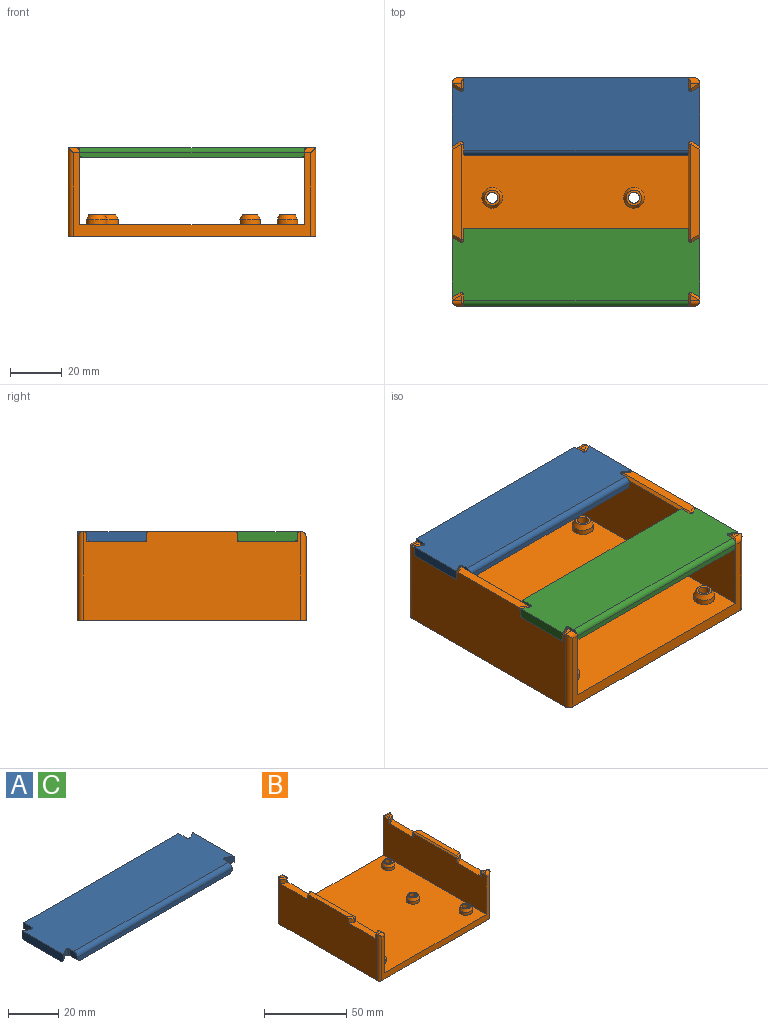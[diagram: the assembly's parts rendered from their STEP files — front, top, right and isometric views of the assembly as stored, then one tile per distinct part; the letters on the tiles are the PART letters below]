
ASSEMBLY  parts=3 mates=2
PART A: 31 faces, bbox 96x30x4 mm
  f0: cylinder r=1mm len=3mm, axis (0,0,1), area 6.3mm2, adj f1,f15,f17,f22
  f1: plane 4.27x3mm, normal (-1,0,0), area 11.9mm2, adj f0,f2,f17,f21,f30
  f2: plane 87x2mm, normal (0,-1,0), area 173mm2, adj f1,f3,f16,f21,f29,f30
  f3: plane 4.27x3mm, normal (1,0,0), area 11.9mm2, adj f2,f4,f17,f29,f30
  f4: cylinder r=1mm len=3mm, axis (0,0,1), area 6.3mm2, adj f3,f5,f17,f28
  f5: plane 3x3mm, normal (-0.5,-0.87,0), area 10.4mm2, adj f4,f6,f17,f27
  f6: plane 23.2x4mm, normal (1,0,0), area 91.6mm2, adj f5,f7,f16,f17,f24,f27
  f7: plane 3x3mm, normal (-0.5,0.87,0), area 10.4mm2, adj f6,f8,f17,f24
  f8: cylinder r=1mm len=3mm, axis (0,0,1), area 6.3mm2, adj f7,f9,f17,f25
  f9: plane 4.27x3mm, normal (1,0,0), area 12.8mm2, adj f8,f10,f17,f26
  f10: plane 87x4mm, normal (0,1,0), area 347mm2, adj f9,f11,f16,f17,f20,f26
  f11: plane 4.27x3mm, normal (-1,0,0), area 12.8mm2, adj f10,f12,f17,f20
  f12: cylinder r=1mm len=3mm, axis (0,0,1), area 6.3mm2, adj f11,f13,f17,f19
  f13: plane 3x3mm, normal (0.5,0.87,0), area 10.4mm2, adj f12,f14,f17,f18
  f14: plane 23.2x4mm, normal (-1,0,0), area 91.6mm2, adj f13,f15,f16,f17,f18,f23
  f15: plane 3x3mm, normal (0.5,-0.87,0), area 10.4mm2, adj f0,f14,f17,f23
  f16: plane 96x30mm, normal (0,0,-1), area 2755.8mm2, adj f2,f6,f10,f14,f18,f19,f20,f21
  f17: plane 96x28mm, normal (0,0,1), area 2624.1mm2, adj f0,f1,f3,f4,f5,f6,f7,f8
  f18: plane 3x2.6mm, normal (0.35,0.61,-0.71), area 4.5mm2, adj f13,f14,f16,f19
  f19: cone r=2mm half-angle=45deg, axis (0,0,-1), area 4.4mm2, adj f12,f16,f18,f20
  f20: plane 4.27x1mm, normal (-0.71,0,-0.71), area 6mm2, adj f10,f11,f16,f19
  f21: plane 4.27x1mm, normal (-0.71,0,-0.71), area 6mm2, adj f1,f2,f16,f22
  f22: cone r=1mm half-angle=45deg, axis (0,0,-1), area 4.4mm2, adj f0,f16,f21,f23
  f23: plane 3x2.6mm, normal (0.35,-0.61,-0.71), area 4.5mm2, adj f14,f15,f16,f22
  f24: plane 3x2.6mm, normal (-0.35,0.61,-0.71), area 4.5mm2, adj f6,f7,f16,f25
  f25: cone r=2mm half-angle=45deg, axis (0,0,-1), area 4.4mm2, adj f8,f16,f24,f26
  f26: plane 4.27x1mm, normal (0.71,0,-0.71), area 6mm2, adj f9,f10,f16,f25
  f27: plane 3x2.6mm, normal (-0.35,-0.61,-0.71), area 4.5mm2, adj f5,f6,f16,f28
  f28: cone r=2mm half-angle=45deg, axis (0,0,-1), area 4.4mm2, adj f4,f16,f27,f29
  f29: plane 4.27x1mm, normal (0.71,0,-0.71), area 6mm2, adj f2,f3,f16,f28
  f30: cylinder r=2mm len=87mm, axis (1,0,0), area 273.3mm2, adj f1,f2,f3,f17
PART B: 268 faces, bbox 96x88.5x34.5 mm
  f0: plane 3.5x2.27mm, normal (0,0,1), area 4.4mm2, adj f2,f246,f248,f264
  f1: plane 37.04x3.5mm, normal (0,0,1), area 122.6mm2, adj f2,f241,f242,f245
  f2: plane 84.5x34.5mm, normal (1,0,0), area 2727.4mm2, adj f0,f1,f5,f6,f228,f230,f231,f233
  f3: plane 3.5x2.27mm, normal (0,0,1), area 4.4mm2, adj f9,f249,f251,f261
  f4: plane 37.04x3.5mm, normal (0,0,1), area 122.6mm2, adj f9,f255,f257,f258
  f5: plane 96x88.5mm, normal (0,0,-1), area 8084.9mm2, adj f2,f7,f8,f9,f16,f19,f22,f25
  f6: plane 3.5x2.27mm, normal (0,0,1), area 4.4mm2, adj f2,f238,f240,f266
  f7: plane 92x32.5mm, normal (0,-1,0), area 554mm2, adj f5,f11,f12,f13,f262,f263,f266,f267
  f8: plane 92x32.5mm, normal (0,1,0), area 554mm2, adj f5,f11,f12,f13,f260,f261,f264,f265
  f9: plane 84.5x34.5mm, normal (-1,0,0), area 2727.4mm2, adj f3,f4,f5,f10,f218,f221,f222,f223
  f10: plane 3.5x2.27mm, normal (0,0,1), area 4.4mm2, adj f9,f252,f253,f263
  f11: plane 88.5x29mm, normal (-1,0,0), area 2437.5mm2, adj f7,f8,f13,f228,f229,f232,f233,f234
  f12: plane 88.5x29mm, normal (1,0,0), area 2437.5mm2, adj f7,f8,f13,f218,f219,f220,f223,f224
  f13: plane 88.5x87mm, normal (0,0,1), area 7397.9mm2, adj f7,f8,f11,f12,f200,f202,f204,f206
  f14: cylinder r=2.12mm len=5mm, axis (0,0,-1), area 66.8mm2, adj f15,f201
  f15: plane 6.5x6.5mm, normal (0,0,-1), area 19mm2, adj f14,f16
  f16: cylinder r=3.25mm len=6.5mm, axis (0,0,-1), area 71.5mm2, adj f5,f15
  f17: cylinder r=2.12mm len=5mm, axis (0,0,-1), area 66.8mm2, adj f18,f211
  f18: plane 6.5x6.5mm, normal (0,0,-1), area 19mm2, adj f17,f19
  f19: cylinder r=3.25mm len=6.5mm, axis (0,0,-1), area 71.5mm2, adj f5,f18
  f20: cylinder r=2.12mm len=5mm, axis (0,0,-1), area 66.8mm2, adj f21,f203
  f21: plane 6.5x6.5mm, normal (0,0,-1), area 19mm2, adj f20,f22
  f22: cylinder r=3.25mm len=6.5mm, axis (0,0,-1), area 71.5mm2, adj f5,f21
  f23: cylinder r=2.12mm len=5mm, axis (0,0,-1), area 66.8mm2, adj f24,f209
  f24: plane 6.5x6.5mm, normal (0,0,-1), area 19mm2, adj f23,f25
  f25: cylinder r=3.25mm len=6.5mm, axis (0,0,-1), area 71.5mm2, adj f5,f24
  f26: cylinder r=2.12mm len=5mm, axis (0,0,-1), area 66.8mm2, adj f27,f207
  f27: plane 6.5x6.5mm, normal (0,0,-1), area 19mm2, adj f26,f28
  f28: cylinder r=3.25mm len=6.5mm, axis (0,0,-1), area 71.5mm2, adj f5,f27
  f29: cylinder r=2.12mm len=5mm, axis (0,0,-1), area 66.8mm2, adj f30,f205
  f30: plane 6.5x6.5mm, normal (0,0,-1), area 19mm2, adj f29,f31
  f31: cylinder r=3.25mm len=6.5mm, axis (0,0,-1), area 71.5mm2, adj f5,f30
  f32: extruded ~1.04x1mm, area 1.1mm2, adj f5,f33,f44,f45
  f33: extruded ~1x0.82mm, area 1.1mm2, adj f5,f32,f34,f45
  f34: plane 1x0.08mm, normal (0,1,0), area 0.1mm2, adj f5,f33,f35,f45
  f35: plane 1.02x1mm, normal (-0.97,0.23,0), area 1mm2, adj f5,f34,f36,f45
  f36: plane 1.25x1mm, normal (0,1,0), area 1.3mm2, adj f5,f35,f37,f45
  f37: plane 6.07x1mm, normal (1,0,0), area 6.1mm2, adj f5,f36,f38,f45
  f38: plane 1.65x1mm, normal (0,-1,0), area 1.7mm2, adj f5,f37,f39,f45
  f39: plane 3.09x1mm, normal (-1,0,0), area 3.1mm2, adj f5,f38,f40,f45
  f40: extruded ~1.14x1mm, area 1.3mm2, adj f5,f39,f41,f45
  f41: extruded ~1.23x1mm, area 1.3mm2, adj f5,f40,f42,f45
  f42: extruded ~1x0.49mm, area 0.5mm2, adj f5,f41,f43,f45
  f43: plane 1.55x1mm, normal (-1,-0.08,0), area 1.6mm2, adj f5,f42,f44,f45
  f44: extruded ~1x0.56mm, area 0.6mm2, adj f5,f32,f43,f45
  f45: plane 6.18x3.94mm, normal (0,0,-1), area 13.2mm2, adj f32,f33,f34,f35,f36,f37,f38,f39
  f46: plane 7.93x1mm, normal (1,0,0), area 7.9mm2, adj f5,f47,f70,f71
  f47: plane 2.97x1mm, normal (0,-1,0), area 3mm2, adj f5,f46,f48,f71
  f48: extruded ~2.13x1mm, area 2.3mm2, adj f5,f47,f49,f71
  f49: extruded ~1.69x1mm, area 1.9mm2, adj f5,f48,f50,f71
  f50: extruded ~1.23x1mm, area 1.3mm2, adj f5,f49,f51,f71
  f51: extruded ~1.09x1mm, area 1.3mm2, adj f5,f50,f52,f71
  f52: plane 1x0.05mm, normal (-1,0,0), area 0.1mm2, adj f5,f51,f53,f71
  f53: extruded ~1x0.89mm, area 1.1mm2, adj f5,f52,f54,f71
  f54: extruded ~1.17x1mm, area 1.2mm2, adj f5,f53,f55,f71
  f55: extruded ~1.53x1mm, area 1.8mm2, adj f5,f54,f56,f71
  f56: extruded ~2.45x1mm, area 2.5mm2, adj f5,f55,f70,f71
  f57: plane 1.76x1mm, normal (-1,0,0), area 1.8mm2, adj f58,f68,f71,f73
  f58: plane 1x0.88mm, normal (0,-1,0), area 0.9mm2, adj f57,f59,f71,f73
  f59: extruded ~1.06x1mm, area 1.1mm2, adj f58,f60,f71,f73
  f60: extruded ~1x0.65mm, area 0.8mm2, adj f59,f61,f71,f73
  f61: extruded ~1x0.7mm, area 0.8mm2, adj f60,f62,f71,f73
  f62: extruded ~1x0.99mm, area 1mm2, adj f61,f68,f71,f73
  f63: plane 1.04x1mm, normal (0,-1,0), area 1mm2, adj f64,f69,f71,f72
  f64: extruded ~1.41x1mm, area 2mm2, adj f63,f65,f71,f72
  f65: extruded ~1x0.81mm, area 0.9mm2, adj f64,f66,f71,f72
  f66: extruded ~1.03x1mm, area 1.1mm2, adj f65,f67,f71,f72
  f67: plane 1.1x1mm, normal (0,1,0), area 1.1mm2, adj f66,f69,f71,f72
  f68: plane 1x0.98mm, normal (0,1,0), area 1mm2, adj f57,f62,f71,f73
  f69: plane 2.07x1mm, normal (-1,0,0), area 2.1mm2, adj f63,f67,f71,f72
  f70: plane 2.47x1mm, normal (0,1,0), area 2.5mm2, adj f5,f46,f56,f71
  f71: plane 7.93x5.88mm, normal (0,0,-1), area 34.3mm2, adj f46,f47,f48,f49,f50,f51,f52,f53
  f72: plane 2.45x2.07mm, normal (0,0,-1), area 4.6mm2, adj f63,f64,f65,f66,f67,f69
  f73: plane 2.27x1.76mm, normal (0,0,-1), area 3.6mm2, adj f57,f58,f59,f60,f61,f62,f68
  f74: extruded ~1x0.84mm, area 0.9mm2, adj f75,f93,f94,f199
  f75: extruded ~1x0.95mm, area 1mm2, adj f74,f76,f94,f199
  f76: plane 2.32x1mm, normal (0,1,0), area 2.3mm2, adj f75,f77,f94,f199
  f77: extruded ~1x0.95mm, area 1mm2, adj f76,f93,f94,f199
  f78: extruded ~1.21x1mm, area 1.2mm2, adj f5,f79,f92,f94
  f79: extruded ~1x0.93mm, area 1mm2, adj f5,f78,f80,f94
  f80: plane 1.28x1mm, normal (-1,0,0), area 1.3mm2, adj f5,f79,f81,f94
  f81: extruded ~1.02x1mm, area 1.1mm2, adj f5,f80,f82,f94
  f82: extruded ~1.04x1mm, area 1mm2, adj f5,f81,f83,f94
  f83: extruded ~1.1x1mm, area 1.2mm2, adj f5,f82,f84,f94
  f84: extruded ~1.1x1mm, area 1.2mm2, adj f5,f83,f85,f94
  f85: plane 3.91x1mm, normal (0,-1,0), area 3.9mm2, adj f5,f84,f86,f94
  f86: plane 1x0.8mm, normal (-1,0,0), area 0.8mm2, adj f5,f85,f87,f94
  f87: extruded ~2.02x1mm, area 2.2mm2, adj f5,f86,f88,f94
  f88: extruded ~2x1mm, area 2.2mm2, adj f5,f87,f89,f94
  f89: extruded ~2.11x1mm, area 2.3mm2, adj f5,f88,f90,f94
  f90: extruded ~2.36x1mm, area 2.5mm2, adj f5,f89,f91,f94
  f91: extruded ~2.29x1mm, area 2.5mm2, adj f5,f90,f92,f94
  f92: extruded ~2.29x1mm, area 2.5mm2, adj f5,f78,f91,f94
  f93: extruded ~1x0.82mm, area 0.9mm2, adj f74,f77,f94,f199
  f94: plane 6.29x5.59mm, normal (0,0,-1), area 22.2mm2, adj f74,f75,f76,f77,f78,f79,f80,f81
  f95: plane 1.41x1mm, normal (-1,0,0), area 1.4mm2, adj f5,f96,f118,f119
  f96: plane 3.46x1mm, normal (0,1,0), area 3.5mm2, adj f5,f95,f97,f119
  f97: plane 1x0.07mm, normal (-1,0,0), area 0.1mm2, adj f5,f96,f98,f119
  f98: plane 1.02x1mm, normal (-0.69,-0.73,0), area 1.4mm2, adj f5,f97,f99,f119
  f99: extruded ~1.44x1.42mm, area 2mm2, adj f5,f98,f100,f119
  f100: extruded ~1x0.98mm, area 1.2mm2, adj f5,f99,f101,f119
  f101: extruded ~1.03x1mm, area 1.1mm2, adj f5,f100,f102,f119
  f102: extruded ~1.12x1mm, area 1.2mm2, adj f5,f101,f103,f119
  f103: extruded ~1x0.88mm, area 1.2mm2, adj f5,f102,f104,f119
  f104: extruded ~1.31x1mm, area 1.4mm2, adj f5,f103,f105,f119
  f105: extruded ~1.02x1mm, area 1mm2, adj f5,f104,f106,f119
  f106: extruded ~1x0.84mm, area 0.9mm2, adj f5,f105,f107,f119
  f107: extruded ~1x0.97mm, area 1.2mm2, adj f5,f106,f108,f119
  f108: plane 1.08x1mm, normal (0.76,-0.65,0), area 1.4mm2, adj f5,f107,f109,f119
  f109: extruded ~1x0.91mm, area 1.1mm2, adj f5,f108,f110,f119
  f110: extruded ~1x0.89mm, area 0.9mm2, adj f5,f109,f111,f119
  f111: extruded ~1x0.7mm, area 0.8mm2, adj f5,f110,f112,f119
  f112: extruded ~1x0.71mm, area 0.8mm2, adj f5,f111,f113,f119
  f113: extruded ~1x0.62mm, area 0.6mm2, adj f5,f112,f114,f119
  f114: extruded ~1x0.65mm, area 0.8mm2, adj f5,f113,f115,f119
  f115: extruded ~1.26x1.16mm, area 1.7mm2, adj f5,f114,f116,f119
  f116: plane 2.01x1.99mm, normal (0.71,0.7,0), area 2.8mm2, adj f5,f115,f117,f119
  f117: plane 1.17x1mm, normal (1,0,0), area 1.2mm2, adj f5,f116,f118,f119
  f118: plane 5.55x1mm, normal (0,-1,0), area 5.5mm2, adj f5,f95,f117,f119
  f119: plane 8.05x5.57mm, normal (0,0,-1), area 23.4mm2, adj f95,f96,f97,f98,f99,f100,f101,f102
  f120: plane 4.72x1.5mm, normal (0.95,0.3,0), area 5mm2, adj f5,f121,f129,f130
  f121: extruded ~1.75x1mm, area 1.8mm2, adj f5,f120,f122,f130
  f122: extruded ~1x0.77mm, area 0.8mm2, adj f5,f121,f123,f130
  f123: extruded ~1x0.97mm, area 1mm2, adj f5,f122,f124,f130
  f124: plane 4.72x1.49mm, normal (-0.95,0.3,0), area 5mm2, adj f5,f123,f125,f130
  f125: plane 1.7x1mm, normal (0,1,0), area 1.7mm2, adj f5,f124,f126,f130
  f126: plane 7.93x2.69mm, normal (0.95,-0.32,0), area 8.4mm2, adj f5,f125,f127,f130
  f127: plane 1.83x1mm, normal (0,-1,0), area 1.8mm2, adj f5,f126,f128,f130
  f128: plane 7.93x2.7mm, normal (-0.95,-0.32,0), area 8.4mm2, adj f5,f127,f129,f130
  f129: plane 1.7x1mm, normal (0,1,0), area 1.7mm2, adj f5,f120,f128,f130
  f130: plane 7.93x7.22mm, normal (0,0,-1), area 24.3mm2, adj f120,f121,f122,f123,f124,f125,f126,f127
  f131: extruded ~1.04x1mm, area 1.1mm2, adj f5,f132,f143,f144
  f132: extruded ~1x0.82mm, area 1.1mm2, adj f5,f131,f133,f144
  f133: plane 1x0.08mm, normal (0,1,0), area 0.1mm2, adj f5,f132,f134,f144
  f134: plane 1.02x1mm, normal (-0.97,0.23,0), area 1mm2, adj f5,f133,f135,f144
  f135: plane 1.25x1mm, normal (0,1,0), area 1.3mm2, adj f5,f134,f136,f144
  f136: plane 6.07x1mm, normal (1,0,0), area 6.1mm2, adj f5,f135,f137,f144
  f137: plane 1.65x1mm, normal (0,-1,0), area 1.7mm2, adj f5,f136,f138,f144
  f138: plane 3.09x1mm, normal (-1,0,0), area 3.1mm2, adj f5,f137,f139,f144
  f139: extruded ~1.14x1mm, area 1.3mm2, adj f5,f138,f140,f144
  f140: extruded ~1.23x1mm, area 1.3mm2, adj f5,f139,f141,f144
  f141: extruded ~1x0.49mm, area 0.5mm2, adj f5,f140,f142,f144
  f142: plane 1.55x1mm, normal (-1,-0.08,0), area 1.6mm2, adj f5,f141,f143,f144
  f143: extruded ~1x0.56mm, area 0.6mm2, adj f5,f131,f142,f144
  f144: plane 6.18x3.94mm, normal (0,0,-1), area 13.2mm2, adj f131,f132,f133,f134,f135,f136,f137,f138
  f145: plane 3.96x1mm, normal (-1,0,0), area 4mm2, adj f5,f146,f161,f162
  f146: extruded ~1.65x1mm, area 1.8mm2, adj f5,f145,f147,f162
  f147: extruded ~1.61x1mm, area 1.8mm2, adj f5,f146,f148,f162
  f148: extruded ~1.1x1mm, area 1.1mm2, adj f5,f147,f149,f162
  f149: extruded ~1x0.76mm, area 1mm2, adj f5,f148,f150,f162
  f150: plane 1x0.09mm, normal (0,1,0), area 0.1mm2, adj f5,f149,f151,f162
  f151: plane 1x0.78mm, normal (-0.96,0.28,0), area 0.8mm2, adj f5,f150,f152,f162
  f152: plane 1.26x1mm, normal (0,1,0), area 1.3mm2, adj f5,f151,f153,f162
  f153: plane 6.07x1mm, normal (1,0,0), area 6.1mm2, adj f5,f152,f154,f162
  f154: plane 1.65x1mm, normal (0,-1,0), area 1.7mm2, adj f5,f153,f155,f162
  f155: plane 2.85x1mm, normal (-1,0,0), area 2.9mm2, adj f5,f154,f156,f162
  f156: extruded ~1.54x1mm, area 1.6mm2, adj f5,f155,f157,f162
  f157: extruded ~1x1mm, area 1.2mm2, adj f5,f156,f158,f162
  f158: extruded ~1x0.74mm, area 0.8mm2, adj f5,f157,f159,f162
  f159: extruded ~1x0.98mm, area 1mm2, adj f5,f158,f160,f162
  f160: plane 3.54x1mm, normal (1,0,0), area 3.5mm2, adj f5,f159,f161,f162
  f161: plane 1.65x1mm, normal (0,-1,0), area 1.7mm2, adj f5,f145,f160,f162
  f162: plane 6.18x5.6mm, normal (0,0,-1), area 22.5mm2, adj f145,f146,f147,f148,f149,f150,f151,f152
  f163: plane 3.96x1mm, normal (-1,0,0), area 4mm2, adj f5,f164,f179,f180
  f164: extruded ~1.65x1mm, area 1.8mm2, adj f5,f163,f165,f180
  f165: extruded ~1.61x1mm, area 1.8mm2, adj f5,f164,f166,f180
  f166: extruded ~1.1x1mm, area 1.1mm2, adj f5,f165,f167,f180
  f167: extruded ~1x0.76mm, area 1mm2, adj f5,f166,f168,f180
  f168: plane 1x0.09mm, normal (0,1,0), area 0.1mm2, adj f5,f167,f169,f180
  f169: plane 1x0.78mm, normal (-0.96,0.28,0), area 0.8mm2, adj f5,f168,f170,f180
  f170: plane 1.26x1mm, normal (0,1,0), area 1.3mm2, adj f5,f169,f171,f180
  f171: plane 6.07x1mm, normal (1,0,0), area 6.1mm2, adj f5,f170,f172,f180
  f172: plane 1.65x1mm, normal (0,-1,0), area 1.7mm2, adj f5,f171,f173,f180
  f173: plane 2.85x1mm, normal (-1,0,0), area 2.9mm2, adj f5,f172,f174,f180
  f174: extruded ~1.54x1mm, area 1.6mm2, adj f5,f173,f175,f180
  f175: extruded ~1x1mm, area 1.2mm2, adj f5,f174,f176,f180
  f176: extruded ~1x0.74mm, area 0.8mm2, adj f5,f175,f177,f180
  f177: extruded ~1x0.98mm, area 1mm2, adj f5,f176,f178,f180
  f178: plane 3.54x1mm, normal (1,0,0), area 3.5mm2, adj f5,f177,f179,f180
  f179: plane 1.65x1mm, normal (0,-1,0), area 1.7mm2, adj f5,f163,f178,f180
  f180: plane 6.18x5.6mm, normal (0,0,-1), area 22.5mm2, adj f163,f164,f165,f166,f167,f168,f169,f170
  f181: plane 1.27x1mm, normal (0,-1,0), area 1.3mm2, adj f5,f182,f197,f198
  f182: plane 6.07x1mm, normal (-1,0,0), area 6.1mm2, adj f5,f181,f183,f198
  f183: plane 1.65x1mm, normal (0,1,0), area 1.7mm2, adj f5,f182,f184,f198
  f184: plane 2.85x1mm, normal (1,0,0), area 2.9mm2, adj f5,f183,f185,f198
  f185: extruded ~1.54x1mm, area 1.6mm2, adj f5,f184,f186,f198
  f186: extruded ~1x1mm, area 1.2mm2, adj f5,f185,f187,f198
  f187: extruded ~1x0.74mm, area 0.8mm2, adj f5,f186,f188,f198
  f188: extruded ~1x0.98mm, area 1mm2, adj f5,f187,f189,f198
  f189: plane 3.54x1mm, normal (-1,0,0), area 3.5mm2, adj f5,f188,f190,f198
  f190: plane 1.65x1mm, normal (0,1,0), area 1.7mm2, adj f5,f189,f191,f198
  f191: plane 3.96x1mm, normal (1,0,0), area 4mm2, adj f5,f190,f192,f198
  f192: extruded ~1.65x1mm, area 1.8mm2, adj f5,f191,f193,f198
  f193: extruded ~1.61x1mm, area 1.8mm2, adj f5,f192,f194,f198
  f194: extruded ~1.11x1mm, area 1.1mm2, adj f5,f193,f195,f198
  f195: extruded ~1x0.75mm, area 1mm2, adj f5,f194,f196,f198
  f196: plane 1x0.09mm, normal (0,-1,0), area 0.1mm2, adj f5,f195,f197,f198
  f197: plane 1x0.78mm, normal (0.96,-0.28,0), area 0.8mm2, adj f5,f181,f196,f198
  f198: plane 6.18x5.6mm, normal (0,0,-1), area 22.5mm2, adj f181,f182,f183,f184,f185,f186,f187,f188
  f199: plane 2.32x1.28mm, normal (0,0,-1), area 2.4mm2, adj f74,f75,f76,f77,f93
  f200: cylinder r=4mm len=8mm, axis (0,0,-1), area 50.3mm2, adj f13,f217
  f201: plane 6x6mm, normal (0,0,1), area 14.1mm2, adj f14,f217
  f202: cylinder r=4mm len=8mm, axis (0,0,-1), area 50.3mm2, adj f13,f212
  f203: plane 6x6mm, normal (0,0,1), area 14.1mm2, adj f20,f212
  f204: cylinder r=4mm len=8mm, axis (0,0,-1), area 50.3mm2, adj f13,f213
  f205: plane 6x6mm, normal (0,0,1), area 14.1mm2, adj f29,f213
  f206: cylinder r=4mm len=8mm, axis (0,0,-1), area 50.3mm2, adj f13,f215
  f207: plane 6x6mm, normal (0,0,1), area 14.1mm2, adj f26,f215
  f208: cylinder r=4mm len=8mm, axis (0,0,-1), area 50.3mm2, adj f13,f216
  f209: plane 6x6mm, normal (0,0,1), area 14.1mm2, adj f23,f216
  f210: cylinder r=4mm len=8mm, axis (0,0,-1), area 50.3mm2, adj f13,f214
  f211: plane 6x6mm, normal (0,0,1), area 14.1mm2, adj f17,f214
  f212: cone r=3mm half-angle=26.6deg, axis (0,0,-1), area 49.2mm2, adj f202,f203
  f213: cone r=3mm half-angle=26.6deg, axis (0,0,-1), area 49.2mm2, adj f204,f205
  f214: cone r=3mm half-angle=26.6deg, axis (0,0,-1), area 49.2mm2, adj f210,f211
  f215: cone r=3mm half-angle=26.6deg, axis (0,0,-1), area 49.2mm2, adj f206,f207
  f216: cone r=3mm half-angle=26.6deg, axis (0,0,-1), area 49.2mm2, adj f208,f209
  f217: cone r=3mm half-angle=26.6deg, axis (0,0,-1), area 49.2mm2, adj f200,f201
  f218: plane 23.2x4.5mm, normal (0,0,1), area 94.1mm2, adj f9,f12,f219,f220,f221,f222
  f219: cylinder r=1mm len=3mm, axis (0,0,1), area 6.3mm2, adj f12,f218,f222,f256
  f220: cylinder r=1mm len=3mm, axis (0,0,1), area 6.3mm2, adj f12,f218,f221,f254
  f221: plane 3x3mm, normal (-0.5,0.87,0), area 10.4mm2, adj f9,f218,f220,f252
  f222: plane 3x3mm, normal (-0.5,-0.87,0), area 10.4mm2, adj f9,f218,f219,f255
  f223: plane 23.2x4.5mm, normal (0,0,1), area 94.1mm2, adj f9,f12,f224,f225,f226,f227
  f224: cylinder r=1mm len=3mm, axis (0,0,1), area 6.3mm2, adj f12,f223,f226,f250
  f225: cylinder r=1mm len=3mm, axis (0,0,1), area 6.3mm2, adj f12,f223,f227,f259
  f226: plane 3x3mm, normal (-0.5,-0.87,0), area 10.4mm2, adj f9,f223,f224,f249
  f227: plane 3x3mm, normal (-0.5,0.87,0), area 10.4mm2, adj f9,f223,f225,f257
  f228: plane 23.2x4.5mm, normal (0,0,1), area 94.1mm2, adj f2,f11,f229,f230,f231,f232
  f229: cylinder r=1mm len=3mm, axis (0,0,1), area 6.3mm2, adj f11,f228,f230,f239
  f230: plane 3x3mm, normal (0.5,0.87,0), area 10.4mm2, adj f2,f228,f229,f238
  f231: plane 3x3mm, normal (0.5,-0.87,0), area 10.4mm2, adj f2,f228,f232,f242
  f232: cylinder r=1mm len=3mm, axis (0,0,1), area 6.3mm2, adj f11,f228,f231,f244
  f233: plane 23.2x4.5mm, normal (0,0,1), area 94.1mm2, adj f2,f11,f234,f235,f236,f237
  f234: cylinder r=1mm len=3mm, axis (0,0,1), area 6.3mm2, adj f11,f233,f235,f243
  f235: plane 3x3mm, normal (0.5,0.87,0), area 10.4mm2, adj f2,f233,f234,f241
  f236: plane 3x3mm, normal (0.5,-0.87,0), area 10.4mm2, adj f2,f233,f237,f246
  f237: cylinder r=1mm len=3mm, axis (0,0,1), area 6.3mm2, adj f11,f233,f236,f247
  f238: plane 3.5x2.89mm, normal (0.35,0.61,0.71), area 5.3mm2, adj f2,f6,f230,f239
  f239: cone r=1mm half-angle=45deg, axis (0,0,-1), area 1.5mm2, adj f229,f238,f240
  f240: plane 4x1mm, normal (-0.71,0,0.71), area 4.9mm2, adj f6,f11,f239,f266
  f241: plane 3.5x2.89mm, normal (0.35,0.61,0.71), area 5.3mm2, adj f1,f2,f235,f243
  f242: plane 3.5x2.89mm, normal (0.35,-0.61,0.71), area 5.3mm2, adj f1,f2,f231,f244
  f243: cone r=1mm half-angle=45deg, axis (0,0,-1), area 1.5mm2, adj f234,f241,f245
  f244: cone r=1mm half-angle=45deg, axis (0,0,-1), area 1.5mm2, adj f232,f242,f245
  f245: plane 37.04x1mm, normal (-0.71,0,0.71), area 52.4mm2, adj f1,f11,f243,f244
  f246: plane 3.5x2.89mm, normal (0.35,-0.61,0.71), area 5.3mm2, adj f0,f2,f236,f247
  f247: cone r=1mm half-angle=45deg, axis (0,0,-1), area 1.5mm2, adj f237,f246,f248
  f248: plane 4x1mm, normal (-0.71,0,0.71), area 4.9mm2, adj f0,f11,f247,f264
  f249: plane 3.5x2.89mm, normal (-0.35,-0.61,0.71), area 5.3mm2, adj f3,f9,f226,f250
  f250: cone r=1mm half-angle=45deg, axis (0,0,-1), area 1.5mm2, adj f224,f249,f251
  f251: plane 4x1mm, normal (0.71,0,0.71), area 4.9mm2, adj f3,f12,f250,f261
  f252: plane 3.5x2.89mm, normal (-0.35,0.61,0.71), area 5.3mm2, adj f9,f10,f221,f254
  f253: plane 4x1mm, normal (0.71,0,0.71), area 4.9mm2, adj f10,f12,f254,f263
  f254: cone r=1mm half-angle=45deg, axis (0,0,-1), area 1.5mm2, adj f220,f252,f253
  f255: plane 3.5x2.89mm, normal (-0.35,-0.61,0.71), area 5.3mm2, adj f4,f9,f222,f256
  f256: cone r=1mm half-angle=45deg, axis (0,0,-1), area 1.5mm2, adj f219,f255,f258
  f257: plane 3.5x2.89mm, normal (-0.35,0.61,0.71), area 5.3mm2, adj f4,f9,f227,f259
  f258: plane 37.04x1mm, normal (0.71,0,0.71), area 52.4mm2, adj f4,f12,f256,f259
  f259: cone r=1mm half-angle=45deg, axis (0,0,-1), area 1.5mm2, adj f225,f257,f258
  f260: cylinder r=2mm len=34.5mm, axis (0,0,-1), area 106.1mm2, adj f5,f8,f9,f261
  f261: cylinder r=2mm len=4.5mm, axis (1,0,0), area 10.5mm2, adj f3,f8,f12,f251,f260
  f262: cylinder r=2mm len=34.5mm, axis (0,0,1), area 106.1mm2, adj f5,f7,f9,f263
  f263: cylinder r=2mm len=4.5mm, axis (-1,0,0), area 10.5mm2, adj f7,f10,f12,f253,f262
  f264: cylinder r=2mm len=4.5mm, axis (1,0,0), area 10.5mm2, adj f0,f8,f11,f248,f265
  f265: cylinder r=2mm len=34.5mm, axis (0,0,1), area 106.1mm2, adj f2,f5,f8,f264
  f266: cylinder r=2mm len=4.5mm, axis (-1,0,0), area 10.5mm2, adj f6,f7,f11,f240,f267
  f267: cylinder r=2mm len=34.5mm, axis (0,0,-1), area 106.1mm2, adj f2,f5,f7,f266
PART C: same geometry as A
PLACE A t=(-0.11,58,0)mm
PLACE B t=(-0.11,-0.5,0)mm
PLACE C t=(-0.11,-0.5,0)mm
MATE fastened C.f14 <-> B.f9  axis (-1,0,0) through (-48.11,-29.75,30.5)mm
MATE fastened A.f14 <-> B.f9  axis (-1,0,0) through (-48.11,28.75,30.5)mm
